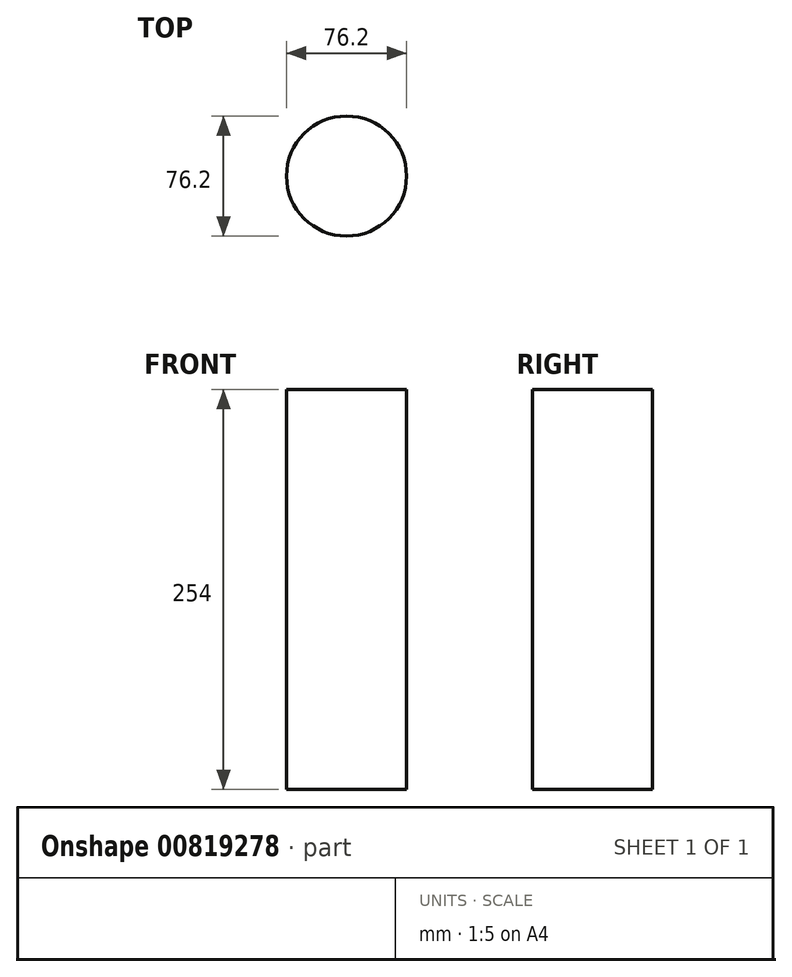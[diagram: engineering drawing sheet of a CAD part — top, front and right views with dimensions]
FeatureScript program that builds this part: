
annotation { "Feature Type Name" : "Feature", "Feature Type Description" : "" }
export const myFeature = defineFeature(function(context is Context, id is Id, definition is map)
    precondition{}
    {
        {
            var Q0;
            Q0=qCreatedBy(makeId("Top.planeOp"),FACE);
            var sketch = newSketch(context, id + "F0", { "sketchPlane" : qUnion([Q0])});
            skCircle(sketch, "E0", {"center": v(0, 0) * mm, "radius": 38.1 * mm});
            skPoint(sketch, "E1", {"position": v(0, -38.1) * mm});
            skSolve(sketch);
        }
        {
            var Q0;
            Q0=sQuery(id+"F0.wireOp",EDGE,"E0");
            extrude(context, id + "F1", {"bodyType" : ToolBodyType.SURFACE, "surfaceEntities" : qUnion([Q0]), "depth" : 254 * mm, "offsetDistance" : 25.4 * mm});
        }
    });
